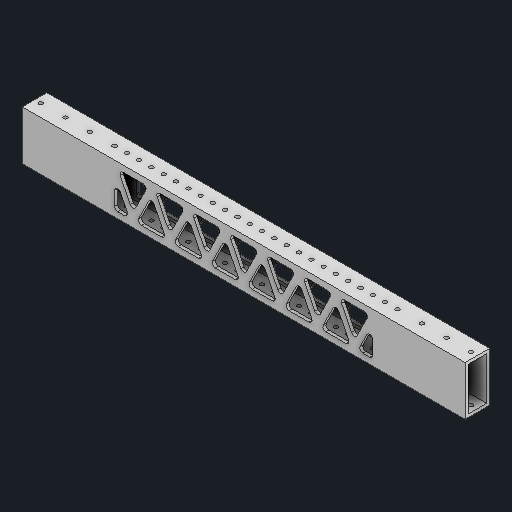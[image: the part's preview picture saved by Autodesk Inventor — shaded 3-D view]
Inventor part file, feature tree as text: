
AUTODESK INVENTOR PART (.ipt)
format: ipt  version: 2023 (Build 270158000, 158)  size: 417,792 bytes
history: native  units: in
note: dims shown in document units (in); Inventor stores cm internally (conversion verified against a paired STEP export)
features: sketch x5, other x3, plane x2
ambient origin geometry x8: Origin, YZ Plane, XZ Plane, XY Plane, X Axis, Y Axis, Z Axis, Center Point
bodies: Solid1 (feature_tree)
feature tree (10):
  other  "fram_extrusion_18in.ipt"
  other  "Solid1::fram_extrusion_18in.ipt"
  other  "TaggingFeature1"
  sketch  "Sketch1"  dims[d0=0.3937in]
  sketch  "Sketch2"
  sketch  "Sketch3"
  sketch  "Sketch4"
  sketch  "Sketch7"
  plane  "Work Plane1"
  plane  "Work Plane2"
